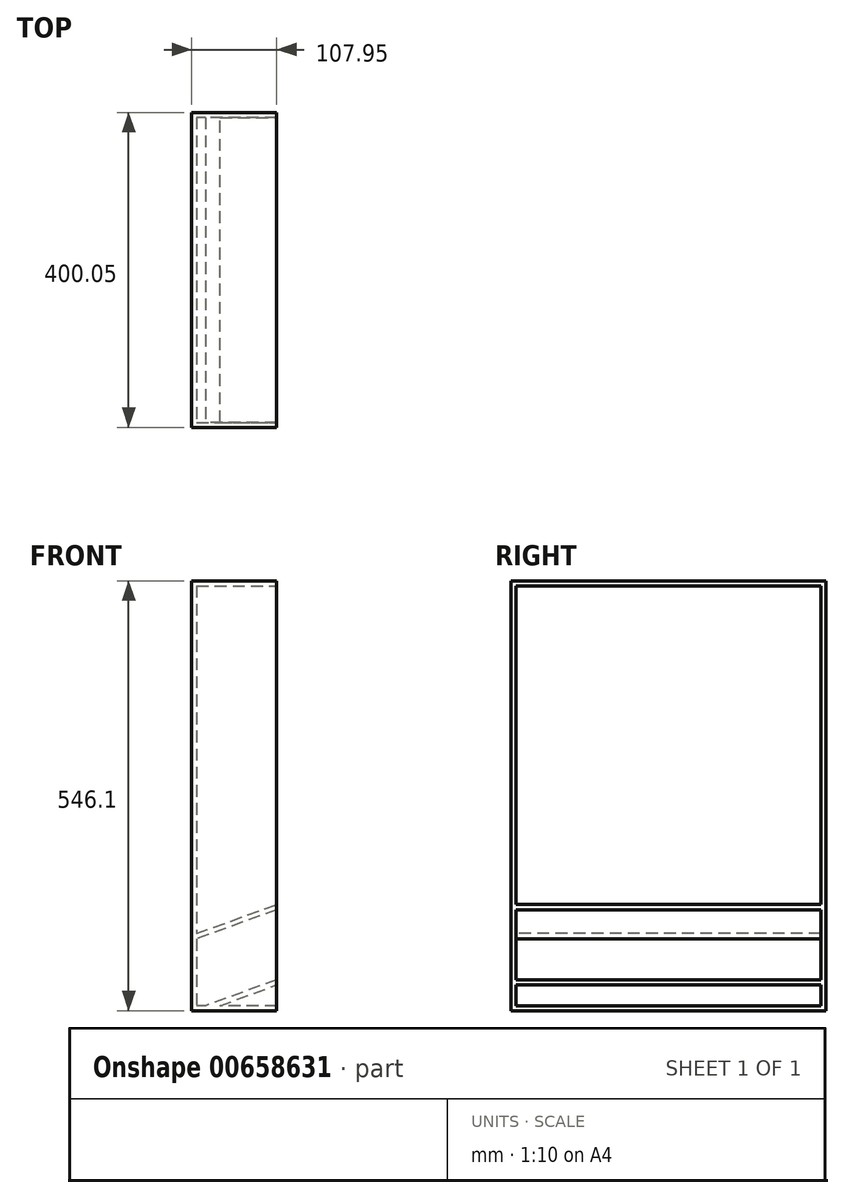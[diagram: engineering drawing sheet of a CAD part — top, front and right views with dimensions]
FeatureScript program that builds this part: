
annotation { "Feature Type Name" : "Feature", "Feature Type Description" : "" }
export const myFeature = defineFeature(function(context is Context, id is Id, definition is map)
    precondition{}
    {
        {
            var Q0;
            Q0=qCreatedBy(makeId("Top.planeOp"),FACE);
            var sketch = newSketch(context, id + "F0", { "sketchPlane" : qUnion([Q0])});
            skLineSegment(sketch, "E0.bottom", {"start": v(0, 0) * mm, "end": v(107.95, 0) * mm});
            skLineSegment(sketch, "E0.top", {"start": v(0, 400.05) * mm, "end": v(107.95, 400.05) * mm});
            skLineSegment(sketch, "E0.left", {"start": v(0, 0) * mm, "end": v(0, 400.05) * mm});
            skLineSegment(sketch, "E0.right", {"start": v(107.95, 0) * mm, "end": v(107.95, 400.05) * mm});
            skSolve(sketch);
        }
        {
            var Q0;
            Q0=makeQuery(id+"F0.imprint","IMPRINT",FACE,{"disambiguationData":[TD([[makeQuery(id+"F0.imprint","IMPRINT",EDGE,{"derivedFrom":sQuery(id+"F0.wireOp",EDGE,"E0.bottom")}),1.0]])]});
            extrude(context, id + "F1", {"entities" : qUnion([Q0]), "depth" : 6.35 * mm, "offsetDistance" : 25.4 * mm});
        }
        {
            var Q0;
            Q0=makeQuery(id+"F1.opExtrude","CAP_FACE",FACE,{"disambiguationData":[OSD([sQuery(id+"F0.wireOp",EDGE,"E0.bottom"),sQuery(id+"F0.wireOp",EDGE,"E0.top"),sQuery(id+"F0.wireOp",EDGE,"E0.left"),sQuery(id+"F0.wireOp",EDGE,"E0.right")])],"isStart":false});
            var sketch = newSketch(context, id + "F2", { "sketchPlane" : qUnion([Q0])});
            skLineSegment(sketch, "E1.bottom", {"start": v(0, 0) * mm, "end": v(107.95, 0) * mm});
            skLineSegment(sketch, "E1.top", {"start": v(0, 6.35) * mm, "end": v(107.95, 6.35) * mm});
            skLineSegment(sketch, "E1.left", {"start": v(0, 0) * mm, "end": v(0, 6.35) * mm});
            skLineSegment(sketch, "E1.right", {"start": v(107.95, 0) * mm, "end": v(107.95, 6.35) * mm});
            skLineSegment(sketch, "E2.bottom", {"start": v(107.95, 400.05) * mm, "end": v(0, 400.05) * mm});
            skLineSegment(sketch, "E2.top", {"start": v(107.95, 393.7) * mm, "end": v(0, 393.7) * mm});
            skLineSegment(sketch, "E2.left", {"start": v(107.95, 400.05) * mm, "end": v(107.95, 393.7) * mm});
            skLineSegment(sketch, "E2.right", {"start": v(0, 400.05) * mm, "end": v(0, 393.7) * mm});
            skSolve(sketch);
        }
        {
            var Q0;
            Q0 = qSketchRegion(id + "F2", true);
            extrude(context, id + "F3", {"entities" : qUnion([Q0]), "operationType" : NewBodyOperationType.ADD, "depth" : 533.4 * mm, "offsetDistance" : 25.4 * mm});
        }
        {
            var Q0;
            Q0=makeQuery(id+"F1.opExtrude","CAP_FACE",FACE,{"disambiguationData":[OSD([sQuery(id+"F0.wireOp",EDGE,"E0.bottom"),sQuery(id+"F0.wireOp",EDGE,"E0.top"),sQuery(id+"F0.wireOp",EDGE,"E0.left"),sQuery(id+"F0.wireOp",EDGE,"E0.right")])],"isStart":false});
            var sketch = newSketch(context, id + "F4", { "sketchPlane" : qUnion([Q0])});
            skLineSegment(sketch, "E3.bottom", {"start": v(0, 393.7) * mm, "end": v(6.35, 393.7) * mm});
            skLineSegment(sketch, "E3.top", {"start": v(0, 6.35) * mm, "end": v(6.35, 6.35) * mm});
            skLineSegment(sketch, "E3.left", {"start": v(0, 393.7) * mm, "end": v(0, 6.35) * mm});
            skLineSegment(sketch, "E3.right", {"start": v(6.35, 393.7) * mm, "end": v(6.35, 6.35) * mm});
            skSolve(sketch);
        }
        {
            var Q0;
            Q0=makeQuery(id+"F4.imprint","IMPRINT",FACE,{"disambiguationData":[TD([[makeQuery(id+"F4.imprint","IMPRINT",EDGE,{"derivedFrom":sQuery(id+"F4.wireOp",EDGE,"E3.bottom")}),1.0]])]});
            extrude(context, id + "F5", {"entities" : qUnion([Q0]), "operationType" : NewBodyOperationType.ADD, "depth" : 533.4 * mm, "offsetDistance" : 25.4 * mm});
        }
        {
            var Q0;
            Q0=makeQuery(id+"F5.boolean.opBoolean","MERGE",FACE,{"derivedFrom":[makeQuery(id+"F3.opExtrude","CAP_FACE",FACE,{"disambiguationData":[OSD([sQuery(id+"F2.wireOp",EDGE,"E1.bottom"),sQuery(id+"F2.wireOp",EDGE,"E1.top"),sQuery(id+"F2.wireOp",EDGE,"E1.left"),sQuery(id+"F2.wireOp",EDGE,"E1.right")])],"isStart":false}),makeQuery(id+"F3.opExtrude","CAP_FACE",FACE,{"disambiguationData":[OSD([sQuery(id+"F2.wireOp",EDGE,"E2.bottom"),sQuery(id+"F2.wireOp",EDGE,"E2.top"),sQuery(id+"F2.wireOp",EDGE,"E2.left"),sQuery(id+"F2.wireOp",EDGE,"E2.right")])],"isStart":false}),makeQuery(id+"F5.opExtrude","CAP_FACE",FACE,{"disambiguationData":[OSD([sQuery(id+"F4.wireOp",EDGE,"E3.bottom"),sQuery(id+"F4.wireOp",EDGE,"E3.top"),sQuery(id+"F4.wireOp",EDGE,"E3.left"),sQuery(id+"F4.wireOp",EDGE,"E3.right")])],"isStart":false})]});
            var sketch = newSketch(context, id + "F6", { "sketchPlane" : qUnion([Q0])});
            skLineSegment(sketch, "E4.bottom", {"start": v(0, 400.05) * mm, "end": v(107.95, 400.05) * mm});
            skLineSegment(sketch, "E4.top", {"start": v(0, 0) * mm, "end": v(107.95, 0) * mm});
            skLineSegment(sketch, "E4.left", {"start": v(0, 400.05) * mm, "end": v(0, 0) * mm});
            skLineSegment(sketch, "E4.right", {"start": v(107.95, 400.05) * mm, "end": v(107.95, 0) * mm});
            skSolve(sketch);
        }
        {
            var Q0;
            Q0 = qSketchRegion(id + "F6", true);
            extrude(context, id + "F7", {"entities" : qUnion([Q0]), "operationType" : NewBodyOperationType.ADD, "depth" : 6.35 * mm, "offsetDistance" : 25.4 * mm});
        }
        {
            var Q0;
            Q0=makeQuery(id+"F3.opExtrude","SWEPT_FACE",FACE,{"disambiguationData":[OSD([sQuery(id+"F2.wireOp",EDGE,"E1.top")])]});
            var sketch = newSketch(context, id + "F8", { "sketchPlane" : qUnion([Q0])});
            skLineSegment(sketch, "E5", {"start": v(0, 0) * mm, "end": v(-18.57, 0) * mm});
            skLineSegment(sketch, "E6", {"start": v(-18.57, 0) * mm, "end": v(-107.95, 32.53) * mm});
            skLineSegment(sketch, "E7", {"start": v(-107.95, 32.53) * mm, "end": v(-107.95, 39.3) * mm});
            skLineSegment(sketch, "E8", {"start": v(-107.95, 39.3) * mm, "end": v(0, 0) * mm});
            skSolve(sketch);
        }
        {
            var Q0;
            Q0 = qSketchRegion(id + "F8", true);
            extrude(context, id + "F9", {"entities" : qUnion([Q0]), "operationType" : NewBodyOperationType.ADD, "depth" : 387.35 * mm, "offsetDistance" : 25.4 * mm});
        }
        {
            var Q0;
            Q0=makeQuery(id+"F9.boolean.opBoolean","SPLIT",FACE,{"disambiguationData":[TD([makeQuery(id+"F5.opExtrude","SWEPT_FACE",FACE,{"disambiguationData":[OSD([sQuery(id+"F4.wireOp",EDGE,"E3.right")])]})])],"derivedFrom":makeQuery(id+"F3.opExtrude","SWEPT_FACE",FACE,{"disambiguationData":[OSD([sQuery(id+"F2.wireOp",EDGE,"E1.top")])]})});
            var sketch = newSketch(context, id + "F10", { "sketchPlane" : qUnion([Q0])});
            skLineSegment(sketch, "E9", {"start": v(-107.95, 128.2) * mm, "end": v(-6.35, 91.21) * mm});
            skLineSegment(sketch, "E10", {"start": v(-6.35, 91.21) * mm, "end": v(-6.35, 97.97) * mm});
            skLineSegment(sketch, "E11", {"start": v(-6.35, 97.97) * mm, "end": v(-107.95, 134.95) * mm});
            skLineSegment(sketch, "E12", {"start": v(-107.95, 134.95) * mm, "end": v(-107.95, 128.2) * mm});
            skSolve(sketch);
        }
        {
            var Q0;
            Q0=makeQuery(id+"F10.imprint","IMPRINT",FACE,{"disambiguationData":[TD([[makeQuery(id+"F10.imprint","IMPRINT",EDGE,{"derivedFrom":sQuery(id+"F10.wireOp",EDGE,"E9")}),1.0]])]});
            extrude(context, id + "F11", {"entities" : qUnion([Q0]), "operationType" : NewBodyOperationType.ADD, "depth" : 387.35 * mm, "offsetDistance" : 25.4 * mm});
        }
    });
